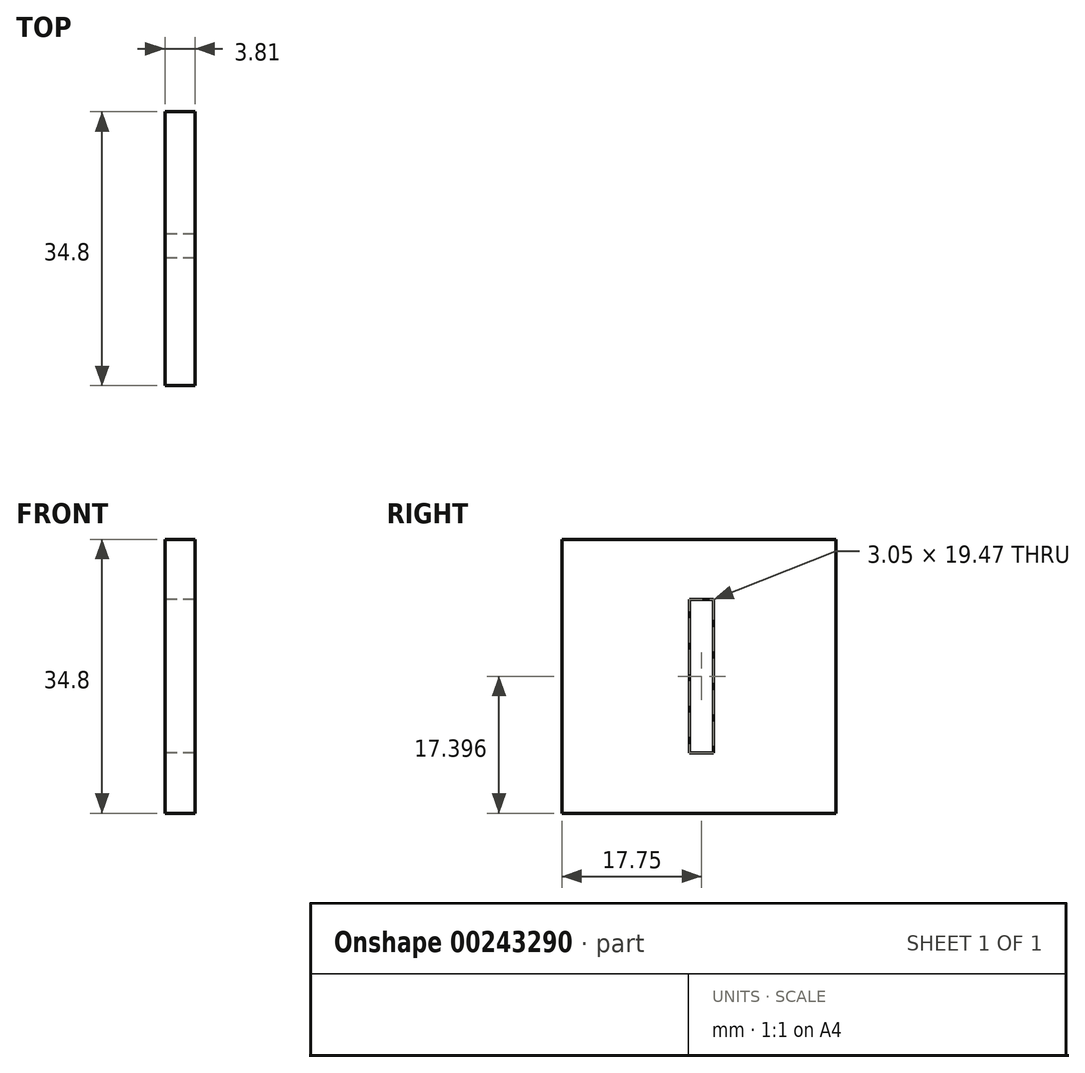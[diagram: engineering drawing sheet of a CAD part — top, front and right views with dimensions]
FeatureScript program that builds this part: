
annotation { "Feature Type Name" : "Feature", "Feature Type Description" : "" }
export const myFeature = defineFeature(function(context is Context, id is Id, definition is map)
    precondition{}
    {
        {
            var Q0;
            Q0=qCreatedBy(makeId("Right.planeOp"),FACE);
            var sketch = newSketch(context, id + "F0", { "sketchPlane" : qUnion([Q0])});
            skLineSegment(sketch, "E0.bottom", {"start": v(-17.75, 26.72) * mm, "end": v(17.05, 26.72) * mm});
            skLineSegment(sketch, "E0.top", {"start": v(-17.75, -8.08) * mm, "end": v(17.05, -8.08) * mm});
            skLineSegment(sketch, "E0.left", {"start": v(-17.75, 26.72) * mm, "end": v(-17.75, -8.08) * mm});
            skLineSegment(sketch, "E0.right", {"start": v(17.05, 26.72) * mm, "end": v(17.05, -8.08) * mm});
            skLineSegment(sketch, "E1.left", {"start": v(-1.52, 19.05) * mm, "end": v(-1.52, 9.32) * mm});
            skLineSegment(sketch, "E2", {"start": v(-1.52, 19.05) * mm, "end": v(0, 19.05) * mm});
            skLineSegment(sketch, "E3.MirrorCS", {"start": v(1.52, 19.05) * mm, "end": v(1.52, 9.32) * mm});
            skLineSegment(sketch, "E4.MirrorCS", {"start": v(1.52, 19.05) * mm, "end": v(0, 19.05) * mm});
            skLineSegment(sketch, "E5", {"start": v(-17.75, 9.32) * mm, "end": v(17.05, 9.32) * mm});
            skLineSegment(sketch, "E6.MirrorCS", {"start": v(1.52, -0.42) * mm, "end": v(1.52, 9.32) * mm});
            skLineSegment(sketch, "E7.MirrorCS", {"start": v(-1.52, -0.42) * mm, "end": v(-1.52, 9.32) * mm});
            skLineSegment(sketch, "E8.MirrorCS", {"start": v(1.52, -0.42) * mm, "end": v(0, -0.42) * mm});
            skLineSegment(sketch, "E9.MirrorCS", {"start": v(-1.52, -0.42) * mm, "end": v(0, -0.42) * mm});
            skSolve(sketch);
        }
        {
            var Q0;
            Q0 = qSketchRegion(id + "F0", true);
            extrude(context, id + "F1", {"entities" : qUnion([Q0]), "depth" : 3.8 * mm});
        }
    });
